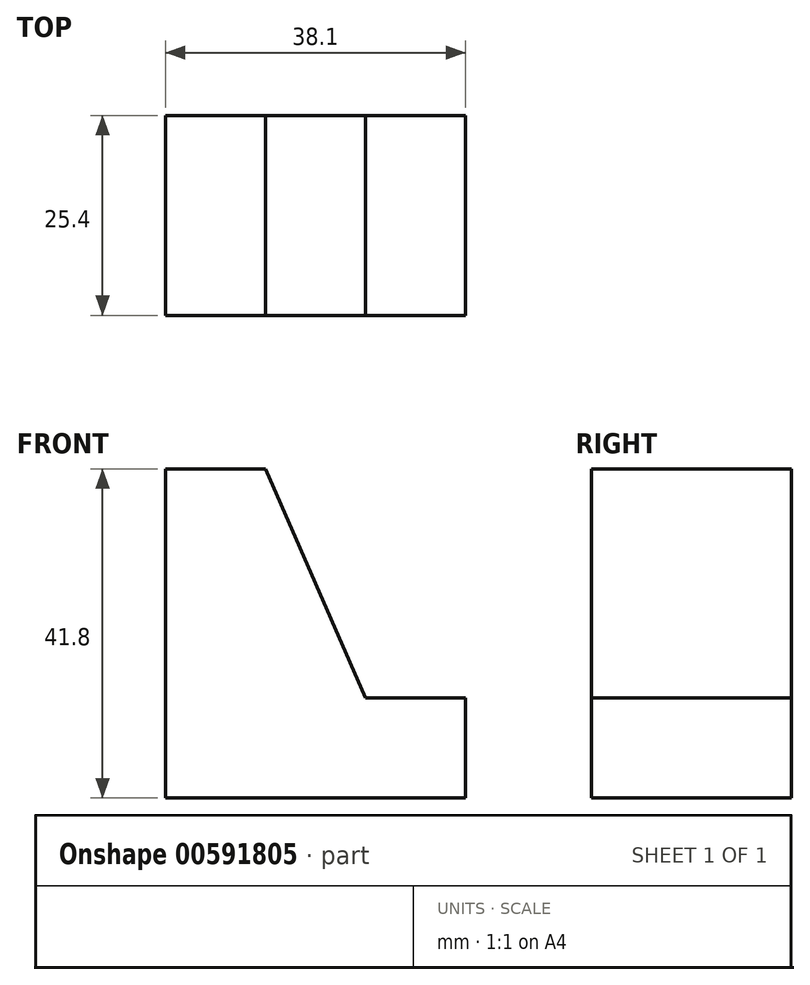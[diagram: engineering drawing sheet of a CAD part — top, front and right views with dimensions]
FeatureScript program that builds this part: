
annotation { "Feature Type Name" : "Feature", "Feature Type Description" : "" }
export const myFeature = defineFeature(function(context is Context, id is Id, definition is map)
    precondition{}
    {
        {
            var Q0;
            Q0=qCreatedBy(makeId("Front.planeOp"),FACE);
            var sketch = newSketch(context, id + "F0", { "sketchPlane" : qUnion([Q0])});
            skLineSegment(sketch, "E0", {"start": v(0, 0) * mm, "end": v(0, 41.8) * mm});
            skLineSegment(sketch, "E1", {"start": v(0, 41.8) * mm, "end": v(12.7, 41.8) * mm});
            skLineSegment(sketch, "E2", {"start": v(12.7, 41.8) * mm, "end": v(25.4, 12.7) * mm});
            skLineSegment(sketch, "E3", {"start": v(25.4, 12.7) * mm, "end": v(38.1, 12.7) * mm});
            skLineSegment(sketch, "E4", {"start": v(38.1, 12.7) * mm, "end": v(38.1, 0) * mm});
            skLineSegment(sketch, "E5", {"start": v(38.1, 0) * mm, "end": v(0, 0) * mm});
            skSolve(sketch);
        }
        {
            var Q0;
            Q0 = qSketchRegion(id + "F0", true);
            extrude(context, id + "F1", {"entities" : qUnion([Q0]), "depth" : 25.4 * mm, "offsetDistance" : 25.4 * mm});
        }
    });
